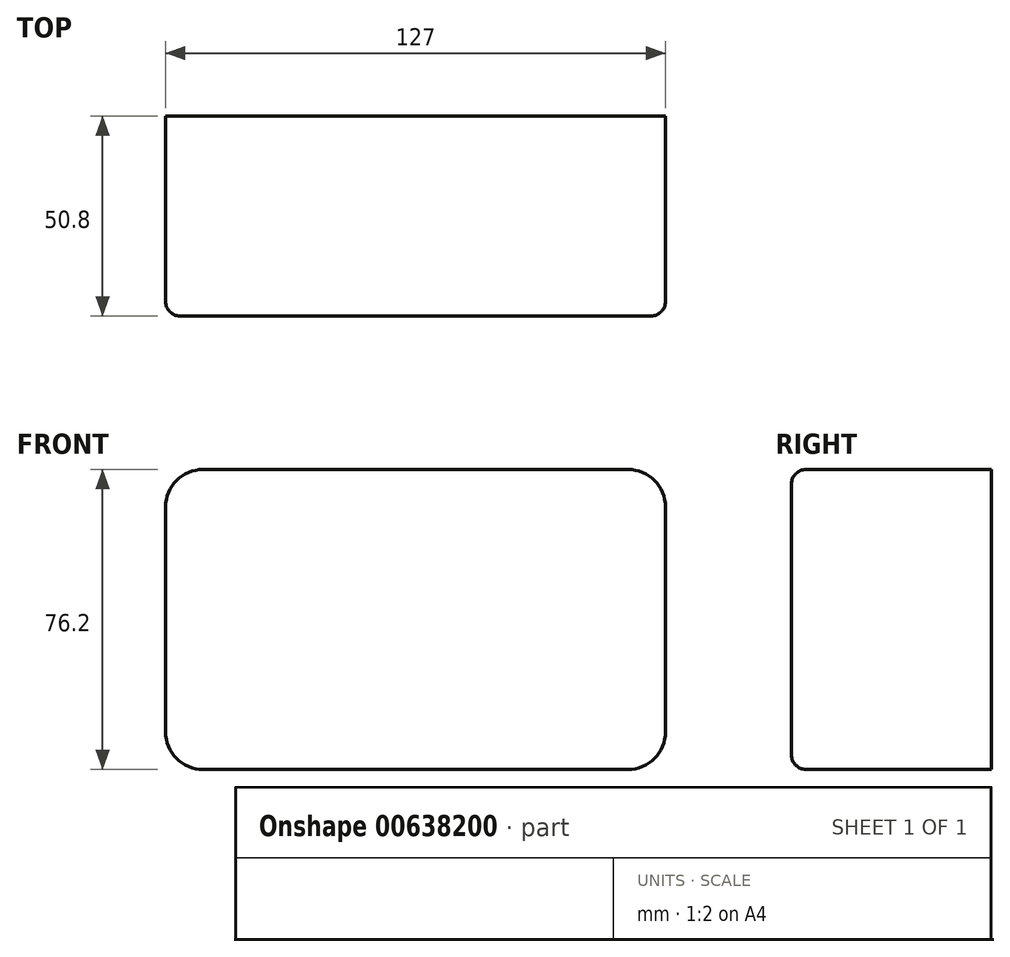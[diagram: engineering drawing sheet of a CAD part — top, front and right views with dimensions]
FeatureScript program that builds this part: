
annotation { "Feature Type Name" : "Feature", "Feature Type Description" : "" }
export const myFeature = defineFeature(function(context is Context, id is Id, definition is map)
    precondition{}
    {
        {
            var Q0;
            Q0=qCreatedBy(makeId("Front.planeOp"),FACE);
            var sketch = newSketch(context, id + "F0", { "sketchPlane" : qUnion([Q0])});
            skLineSegment(sketch, "E0.bottom", {"start": v(53.98, 38.1) * mm, "end": v(-53.98, 38.1) * mm});
            skLineSegment(sketch, "E0.top", {"start": v(53.98, -38.1) * mm, "end": v(-53.98, -38.1) * mm});
            skLineSegment(sketch, "E0.left", {"start": v(63.5, 28.58) * mm, "end": v(63.5, -28.58) * mm});
            skLineSegment(sketch, "E0.right", {"start": v(-63.5, 28.57) * mm, "end": v(-63.5, -28.58) * mm});
            skPoint(sketch, "E0.middle", {"position": v(0, 0) * mm});
            skPoint(sketch, "E1.visualSharp", {"position": v(-63.5, 38.1) * mm});
            skArc(sketch, "E1.filletArc", {"start": v(-53.98, 38.1) * mm, "mid": v(-60.71, 35.31) * mm, "end": v(-63.5, 28.57) * mm});
            skPoint(sketch, "E2.visualSharp", {"position": v(-63.5, -38.1) * mm});
            skArc(sketch, "E2.filletArc", {"start": v(-63.5, -28.58) * mm, "mid": v(-60.71, -35.31) * mm, "end": v(-53.98, -38.1) * mm});
            skPoint(sketch, "E3.visualSharp", {"position": v(63.5, -38.1) * mm});
            skArc(sketch, "E3.filletArc", {"start": v(53.98, -38.1) * mm, "mid": v(60.71, -35.31) * mm, "end": v(63.5, -28.58) * mm});
            skPoint(sketch, "E4.visualSharp", {"position": v(63.5, 38.1) * mm});
            skArc(sketch, "E4.filletArc", {"start": v(63.5, 28.58) * mm, "mid": v(60.71, 35.31) * mm, "end": v(53.98, 38.1) * mm});
            skSolve(sketch);
        }
        {
            var Q0;
            Q0=makeQuery(id+"F0.imprint","IMPRINT",FACE,{"disambiguationData":[TD([[makeQuery(id+"F0.imprint","IMPRINT",EDGE,{"derivedFrom":sQuery(id+"F0.wireOp",EDGE,"E0.bottom")}),1.0]])]});
            extrude(context, id + "F1", {"entities" : qUnion([Q0]), "endBound" : BoundingType.SYMMETRIC, "oppositeDirection" : true, "depth" : 50.8 * mm, "offsetDistance" : 25.4 * mm});
        }
        {
            var Q0;
            Q0=makeQuery(id+"F1.opExtrude","CAP_EDGE",EDGE,{"disambiguationData":[OSD([sQuery(id+"F0.wireOp",EDGE,"E0.bottom")])],"isStart":true});
            fillet(context, id + "F2", {"entities" : qUnion([Q0]), "radius" : 3.68 * mm, "tangentPropagation" : true, "allowEdgeOverflow" : false});
        }
    });
